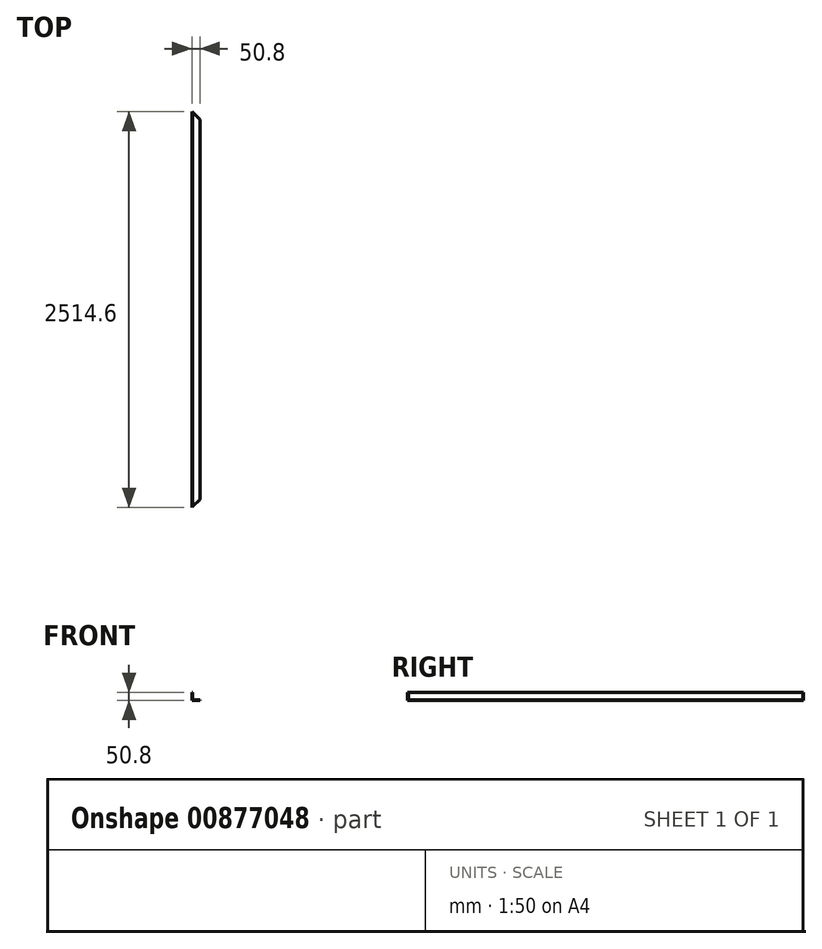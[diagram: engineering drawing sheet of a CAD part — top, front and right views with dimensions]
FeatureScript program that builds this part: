
annotation { "Feature Type Name" : "Feature", "Feature Type Description" : "" }
export const myFeature = defineFeature(function(context is Context, id is Id, definition is map)
    precondition{}
    {
        {
            var Q0;
            Q0=qCreatedBy(makeId("Front.planeOp"),FACE);
            var sketch = newSketch(context, id + "F0", { "sketchPlane" : qUnion([Q0])});
            skLineSegment(sketch, "E0", {"start": v(0, 0) * mm, "end": v(0, 50.8) * mm});
            skLineSegment(sketch, "E1", {"start": v(0, 50.8) * mm, "end": v(4.76, 50.8) * mm});
            skLineSegment(sketch, "E2", {"start": v(4.76, 50.8) * mm, "end": v(4.76, 4.76) * mm});
            skLineSegment(sketch, "E3", {"start": v(4.76, 4.76) * mm, "end": v(50.8, 4.76) * mm});
            skLineSegment(sketch, "E4", {"start": v(50.8, 4.76) * mm, "end": v(50.8, 0) * mm});
            skLineSegment(sketch, "E5", {"start": v(50.8, 0) * mm, "end": v(0, 0) * mm});
            skSolve(sketch);
        }
        {
            var Q0;
            Q0 = qSketchRegion(id + "F0", true);
            extrude(context, id + "F1", {"entities" : qUnion([Q0]), "endBound" : BoundingType.SYMMETRIC, "depth" : 2514.6 * mm, "offsetDistance" : 25.4 * mm});
        }
        {
            var Q0;
            Q0=makeQuery(id+"F1.opExtrude","SWEPT_FACE",FACE,{"disambiguationData":[OSD([sQuery(id+"F0.wireOp",EDGE,"E5")])]});
            var sketch = newSketch(context, id + "F2", { "sketchPlane" : qUnion([Q0])});
            skLineSegment(sketch, "E6", {"start": v(0, 1257.3) * mm, "end": v(50.8, 1206.5) * mm});
            skLineSegment(sketch, "E7", {"start": v(50.8, 1206.5) * mm, "end": v(50.8, 1257.3) * mm});
            skLineSegment(sketch, "E8", {"start": v(50.8, 1257.3) * mm, "end": v(0, 1257.3) * mm});
            skLineSegment(sketch, "E9", {"start": v(0, 0) * mm, "end": v(50.8, 0) * mm, "construction": true});
            skLineSegment(sketch, "E10.MirrorCS", {"start": v(50.8, -1257.3) * mm, "end": v(0, -1257.3) * mm});
            skLineSegment(sketch, "E11.MirrorCS", {"start": v(0, -1257.3) * mm, "end": v(50.8, -1206.5) * mm});
            skLineSegment(sketch, "E12.MirrorCS", {"start": v(50.8, -1206.5) * mm, "end": v(50.8, -1257.3) * mm});
            skSolve(sketch);
        }
        {
            var Q0;
            Q0 = qSketchRegion(id + "F2", true);
            extrude(context, id + "F3", {"entities" : qUnion([Q0]), "operationType" : NewBodyOperationType.REMOVE, "endBound" : BoundingType.THROUGH_ALL, "oppositeDirection" : true, "depth" : 25.4 * mm, "offsetDistance" : 25.4 * mm});
        }
    });
